# Revit family: 3-408-xxx - Pivot CCT
name_source: partatom
category: Luminarias
units: mm (PartAtom-declared; Revit-internal decimal feet)

## family parameters
Anfitrión = Techo
Compartido = No
Corte con vacíos al cargar = No
Cota de conector redondo = Diámetro de uso
Número OmniClass = 23.80.70.11
Origen de luz = Sí
Punto de cálculo de habitación = No
Siempre vertical = Sí
Tipo de pieza = Normal
Título OmniClass = Luminaries for Internal Lighting

## types (1)
- 3-408-40 / Black - Aged Brass
    Cambio de temperatura de color de luz atenuada = <Ninguno>
    Diffusers = White Frost Glass
    Diámetro de círculo de emisión = 610 mm
    Elevación por defecto = 0 mm  [stored 0 ft]
    Exterior Ring = 15 - Black
    Fabricante = Oxygen - Lighting & Fans
    Filtro de color = 16777215
    Forma visible en renderización = No
    Metal Finish = 40 - Aged Brass
    Modelo = 3-408-xx Pivot Pendant
    References = Ref. 3 = 120 V / Ref. 37 = 277 V
    Tamaño de símbolo de origen de luz = 610 mm
    URL = www.oxygenlighting.com
    Voltage = 120 V
    Voltage Input = 120 V or 277 V - 50/60 Hz

note: [stored X ft] marks values corroborated as IEEE doubles in the binary element streams (Revit-internal decimal feet)

## geometry (parser evidence)
native form markers: Sweep x5
no freeform markers — native parametric forms only
